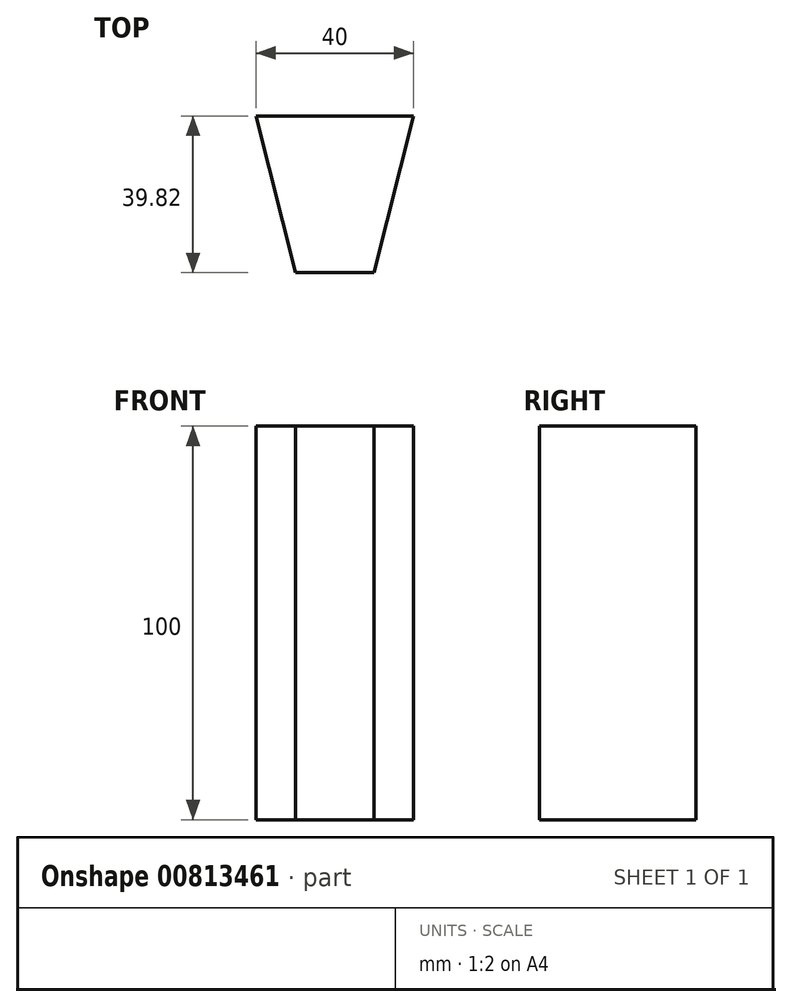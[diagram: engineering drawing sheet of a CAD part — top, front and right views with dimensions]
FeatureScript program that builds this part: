
annotation { "Feature Type Name" : "Feature", "Feature Type Description" : "" }
export const myFeature = defineFeature(function(context is Context, id is Id, definition is map)
    precondition{}
    {
        {
            var Q0;
            Q0=qCreatedBy(makeId("Top.planeOp"),FACE);
            var sketch = newSketch(context, id + "F0", { "sketchPlane" : qUnion([Q0])});
            skLineSegment(sketch, "E0", {"start": v(-10, 0) * mm, "end": v(10, 0) * mm});
            skLineSegment(sketch, "E1", {"start": v(0, 39.82) * mm, "end": v(-20, 39.82) * mm});
            skLineSegment(sketch, "E2", {"start": v(0, 39.82) * mm, "end": v(20, 39.82) * mm});
            skLineSegment(sketch, "E3", {"start": v(-20, 39.82) * mm, "end": v(-10, 0) * mm});
            skLineSegment(sketch, "E4", {"start": v(10, 0) * mm, "end": v(20, 39.82) * mm});
            skSolve(sketch);
        }
        {
            var Q0;
            Q0=makeQuery(id+"F0.imprint","IMPRINT",FACE,{"disambiguationData":[TD([[makeQuery(id+"F0.imprint","IMPRINT",EDGE,{"derivedFrom":sQuery(id+"F0.wireOp",EDGE,"E0")}),1.0]])]});
            extrude(context, id + "F1", {"entities" : qUnion([Q0]), "depth" : 100 * mm, "offsetDistance" : 25 * mm});
        }
    });
